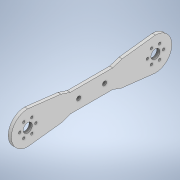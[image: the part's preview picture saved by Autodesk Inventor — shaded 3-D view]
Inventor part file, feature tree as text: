
AUTODESK INVENTOR PART (.ipt)
format: ipt  version: 2022 (Build 260153000, 153)  size: 159,232 bytes
history: native  units: mm
features: extrude x1, sketch x1
ambient origin geometry x8: Origin, YZ Plane, XZ Plane, XY Plane, X Axis, Y Axis, Z Axis, Center Point
bodies: Solid1 (feature_tree)
feature tree (2):
  extrude  "Extrusion1"  [1 undecoded]
  sketch  "Sketch1"  dims[d1=60.0mm d3=8.75mm d4=18.0mm d5=1.2mm d6=4.0mm d7=360.0deg d8=45.0mm d9=8.0mm d10=9.0mm d11=9.0mm d13=8.0mm d14=12.5mm d16=3.0mm d17=0.0mm]
note: 1 required parameter value undecoded (feature->parameter linkage not recoverable at this tier; creation-order binding heuristic only, values carry confidence <= 0.55)
